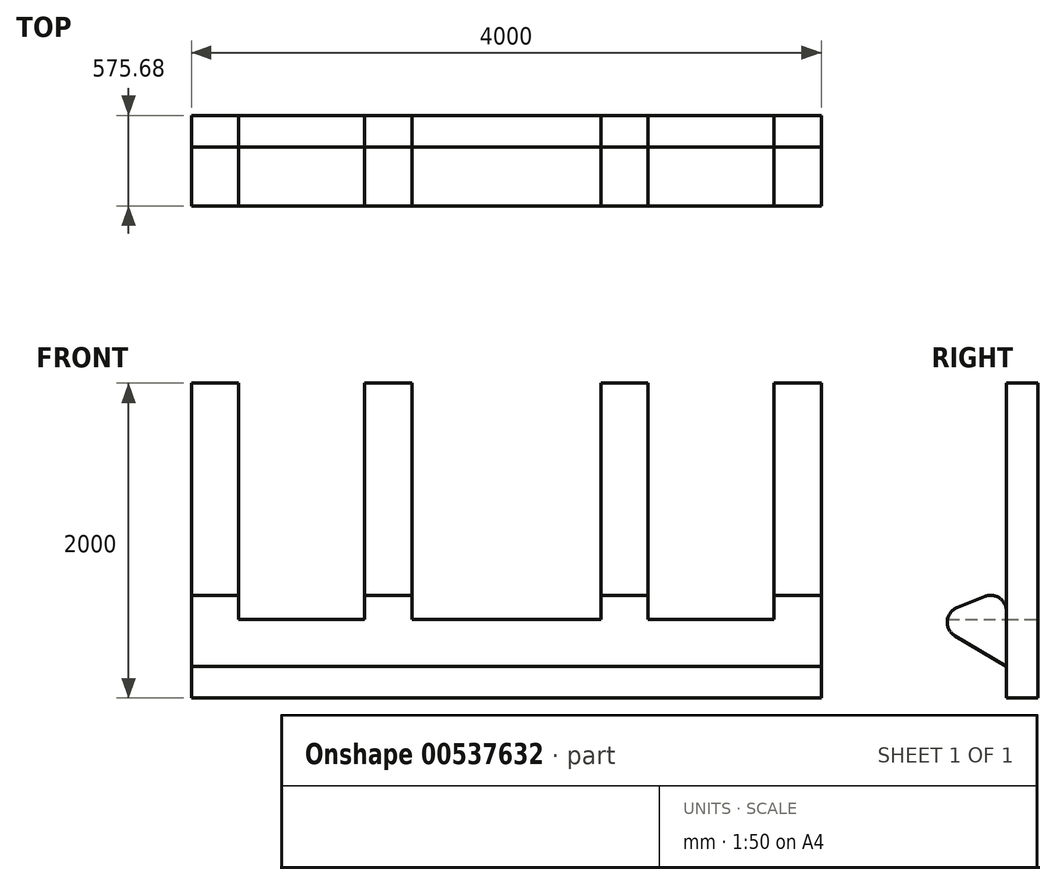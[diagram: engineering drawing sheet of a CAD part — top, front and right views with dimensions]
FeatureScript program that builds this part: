
annotation { "Feature Type Name" : "Feature", "Feature Type Description" : "" }
export const myFeature = defineFeature(function(context is Context, id is Id, definition is map)
    precondition{}
    {
        {
            var Q0;
            Q0=qCreatedBy(makeId("Front.planeOp"),FACE);
            var sketch = newSketch(context, id + "F0", { "sketchPlane" : qUnion([Q0])});
            skLineSegment(sketch, "E0.bottom", {"start": v(-4000, 2000) * mm, "end": v(0, 2000) * mm});
            skLineSegment(sketch, "E0.top", {"start": v(-4000, 0) * mm, "end": v(0, 0) * mm});
            skLineSegment(sketch, "E0.left", {"start": v(-4000, 2000) * mm, "end": v(-4000, 0) * mm});
            skLineSegment(sketch, "E0.right", {"start": v(0, 2000) * mm, "end": v(0, 0) * mm});
            skSolve(sketch);
        }
        {
            var Q0;
            Q0=makeQuery(id+"F0.imprint","IMPRINT",FACE,{"disambiguationData":[TD([[makeQuery(id+"F0.imprint","IMPRINT",EDGE,{"derivedFrom":sQuery(id+"F0.wireOp",EDGE,"E0.bottom")}),-1.0]])]});
            extrude(context, id + "F1", {"entities" : qUnion([Q0]), "depth" : 200 * mm, "offsetDistance" : 25 * mm});
        }
        {
            var Q0;
            Q0=qCreatedBy(makeId("Right.planeOp"),FACE);
            var sketch = newSketch(context, id + "F2", { "sketchPlane" : qUnion([Q0])});
            skLineSegment(sketch, "E1", {"start": v(-200, 200) * mm, "end": v(-700, 500) * mm});
            skLineSegment(sketch, "E2", {"start": v(-700, 500) * mm, "end": v(-200, 700) * mm});
            skLineSegment(sketch, "E3", {"start": v(-200, 700) * mm, "end": v(-200, 200) * mm});
            skSolve(sketch);
        }
        {
            var Q0;
            Q0 = qSketchRegion(id + "F2", true);
            var Q1;
            Q1=makeQuery(id+"F1.opExtrude","SWEPT_FACE",FACE,{"disambiguationData":[OSD([sQuery(id+"F0.wireOp",EDGE,"E0.left")])]});
            extrude(context, id + "F3", {"entities" : qUnion([Q0]), "endBound" : BoundingType.UP_TO_SURFACE, "oppositeDirection" : true, "depth" : 25 * mm, "endBoundEntityFace" : qUnion([Q1]), "offsetDistance" : 25 * mm});
        }
        {
            var Q0;
            Q0=makeQuery(id+"F3.opExtrude","SWEPT_EDGE",EDGE,{"disambiguationData":[OSD([sQuery(id+"F2.wireOp",EDGE,"E1"),sQuery(id+"F2.wireOp",EDGE,"E2")])]});
            fillet(context, id + "F4", {"entities" : qUnion([Q0]), "radius" : 100 * mm, "tangentPropagation" : true, "allowEdgeOverflow" : false});
        }
        {
            var Q0;
            Q0=makeQuery(id+"F3.opExtrude","SWEPT_EDGE",EDGE,{"disambiguationData":[OSD([sQuery(id+"F2.wireOp",EDGE,"E2"),sQuery(id+"F2.wireOp",EDGE,"E3")])]});
            fillet(context, id + "F5", {"entities" : qUnion([Q0]), "radius" : 100 * mm, "tangentPropagation" : true, "allowEdgeOverflow" : false});
        }
        {
            var Q0;
            Q0=makeQuery(id+"F0.imprint","IMPRINT",FACE,{"disambiguationData":[TD([[makeQuery(id+"F0.imprint","IMPRINT",EDGE,{"derivedFrom":sQuery(id+"F0.wireOp",EDGE,"E0.bottom")}),-1.0]])]});
            var sketch = newSketch(context, id + "F6", { "sketchPlane" : qUnion([Q0])});
            skLineSegment(sketch, "E4.bottom", {"start": v(-300, 2000) * mm, "end": v(-1100, 2000) * mm});
            skLineSegment(sketch, "E4.top", {"start": v(-300, 500) * mm, "end": v(-1100, 500) * mm});
            skLineSegment(sketch, "E4.left", {"start": v(-300, 2000) * mm, "end": v(-300, 500) * mm});
            skLineSegment(sketch, "E4.right", {"start": v(-1100, 2000) * mm, "end": v(-1100, 500) * mm});
            skLineSegment(sketch, "E5.bottom", {"start": v(-1400, 2000) * mm, "end": v(-2600, 2000) * mm});
            skLineSegment(sketch, "E5.top", {"start": v(-1400, 500) * mm, "end": v(-2600, 500) * mm});
            skLineSegment(sketch, "E5.left", {"start": v(-1400, 2000) * mm, "end": v(-1400, 500) * mm});
            skLineSegment(sketch, "E5.right", {"start": v(-2600, 2000) * mm, "end": v(-2600, 500) * mm});
            skLineSegment(sketch, "E6.bottom", {"start": v(-2900, 2000) * mm, "end": v(-3700, 2000) * mm});
            skLineSegment(sketch, "E6.top", {"start": v(-2900, 500) * mm, "end": v(-3700, 500) * mm});
            skLineSegment(sketch, "E6.left", {"start": v(-2900, 2000) * mm, "end": v(-2900, 500) * mm});
            skLineSegment(sketch, "E6.right", {"start": v(-3700, 2000) * mm, "end": v(-3700, 500) * mm});
            skSolve(sketch);
        }
        {
            var Q0;
            Q0 = qSketchRegion(id + "F6", true);
            extrude(context, id + "F7", {"entities" : qUnion([Q0]), "operationType" : NewBodyOperationType.REMOVE, "endBound" : BoundingType.THROUGH_ALL, "depth" : 25 * mm, "offsetDistance" : 25 * mm});
        }
    });
